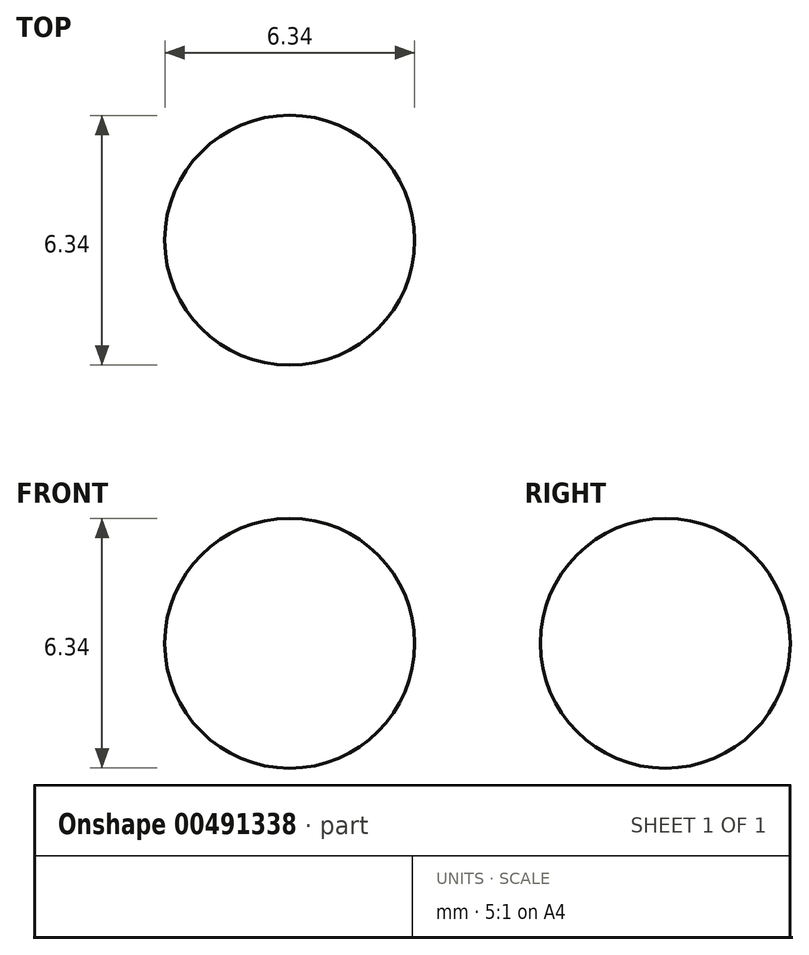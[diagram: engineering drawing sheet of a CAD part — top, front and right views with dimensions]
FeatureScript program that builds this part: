
annotation { "Feature Type Name" : "Feature", "Feature Type Description" : "" }
export const myFeature = defineFeature(function(context is Context, id is Id, definition is map)
    precondition{}
    {
        {
            var Q0;
            Q0=qCreatedBy(makeId("Front.planeOp"),FACE);
            var sketch = newSketch(context, id + "F0", { "sketchPlane" : qUnion([Q0])});
            skLineSegment(sketch, "E0", {"start": v(0, -3.18) * mm, "end": v(0, 3.18) * mm});
            skArc(sketch, "E1", {"start": v(0, -3.18) * mm, "mid": v(3.18, 0) * mm, "end": v(0, 3.18) * mm});
            skSolve(sketch);
        }
        {
            var Q0;
            Q0=makeQuery(id+"F0.imprint","IMPRINT",FACE,{"disambiguationData":[TD([[makeQuery(id+"F0.imprint","IMPRINT",EDGE,{"derivedFrom":sQuery(id+"F0.wireOp",EDGE,"E0")}),-1.0]])]});
            var Q1;
            Q1=sQuery(id+"F0.wireOp",EDGE,"E0");
            revolve(context, id + "F1", {"entities" : qUnion([Q0]), "axis" : qUnion([Q1]), "revolveType" : RevolveType.FULL});
        }
    });
